# Revit family: 306_3370fe3ddf954dd49679af15ecbe6b
name_source: partatom
category: Pipe Accessories
units: mm (PartAtom-declared; Revit-internal decimal feet)

## family parameters
Always vertical = Yes
Cut with Voids When Loaded = No
Part Type = Valve - Breaks Into
Round Connector Dimension = Use Diameter
Shared = No
Work Plane-Based = No

## types (4) — shared parameters
CAT0 = Yes
Description = 2-way Control valve with pressure balanced plug VLE222, PN16 external thread
L2D_Min = 3048 mm
Manufacturer = ESBE
QmdConnectorList = 301;D;302;D
URL = http://www.esbe.eu
Z4 = 13 mm  [stored 0.0426509 ft]
Z5 = 4 mm  [stored 0.0131234 ft]
Z6 = 2 mm  [stored 0.00656168 ft]
Z7 = 15 mm  [stored 0.0492126 ft]
magiPartTypeId = 306
magiProductFamilyId = 3370fe3ddf954dd49679af15ecbe6b

## per-type parameters (varying)
- VLE222 PN16 G1 1/2 DN25-10: CenSd_D6_6=13 mm  [stored 0.0426509 ft]; D=25 mm; D1=29 mm; D13=13 mm  [stored 0.0426509 ft]; D2=24 mm; D3=21 mm; D4=19 mm; D5=20 mm  [stored 0.0656168 ft]; D6=15 mm  [stored 0.0492126 ft]; D7=11 mm; D8=5 mm  [stored 0.0164042 ft]; D9=5 mm  [stored 0.0164042 ft]; DN=20 mm  [stored 0.0656168 ft]; DN1=17 mm  [stored 0.0557743 ft]; DN2=15 mm  [stored 0.0492126 ft]; H3=78 mm; H4=34 mm  [stored 0.111549 ft]; L2=78 mm; L2D=105 mm; LT2=53 mm  [stored 0.173885 ft]; W2D=25 mm  [stored 0.082021 ft]; X1=3 mm  [stored 0.00984252 ft]; XN=11 mm; XN__ve=-11 mm; Z11=9 mm  [stored 0.0295276 ft]; Z14=39 mm; Z2=51 mm  [stored 0.167323 ft]; magiProductId=2265d16c8a8e4a0798807a2ac3ad55
- VLE222 PN16 G2 DN32-16: CenSd_D6_6=13 mm  [stored 0.0426509 ft]; D=32 mm; D1=29 mm; D13=13 mm  [stored 0.0426509 ft]; D2=24 mm; D3=21 mm; D4=19 mm; D5=20 mm  [stored 0.0656168 ft]; D6=15 mm  [stored 0.0492126 ft]; D7=11 mm; D8=5 mm  [stored 0.0164042 ft]; D9=5 mm  [stored 0.0164042 ft]; DN=25 mm  [stored 0.082021 ft]; DN1=21 mm; DN2=19 mm; H3=81 mm; H4=35 mm  [stored 0.114829 ft]; L2=78 mm; L2D=105 mm; LT2=53 mm  [stored 0.173885 ft]; W2D=32 mm  [stored 0.104987 ft]; X1=3 mm  [stored 0.00984252 ft]; XN=11 mm; XN__ve=-11 mm; Z11=9 mm  [stored 0.0295276 ft]; Z14=41 mm; Z2=53 mm  [stored 0.173885 ft]; magiProductId=eaebc783e35940a1959392541471b1
- VLE222 PN16 G2 3/4 DN50-38: CenSd_D6_6=19 mm; D=50 mm; D1=42 mm  [stored 0.137795 ft]; D13=18 mm; D2=34 mm  [stored 0.111549 ft]; D3=30 mm  [stored 0.0984252 ft]; D4=27 mm; D5=29 mm; D6=22 mm; D7=15 mm  [stored 0.0492126 ft]; D8=8 mm  [stored 0.0262467 ft]; D9=7 mm  [stored 0.0229659 ft]; DN=40 mm  [stored 0.131234 ft]; DN1=34 mm  [stored 0.111549 ft]; DN2=30 mm  [stored 0.0984252 ft]; H3=80 mm; H4=53 mm  [stored 0.173885 ft]; L2=111 mm; L2D=150 mm; LT2=75 mm; W2D=50 mm  [stored 0.164042 ft]; X1=5 mm  [stored 0.0164042 ft]; XN=15 mm  [stored 0.0492126 ft]; XN__ve=-15 mm  [stored -0.0492126 ft]; Z11=13 mm  [stored 0.0426509 ft]; Z14=30 mm  [stored 0.0984252 ft]; Z2=80 mm; magiProductId=a5fd4d7e4d3149f6a6e4df05a8dac0
- VLE222 PN16 G2 1/4 DN40-25: CenSd_D6_6=16 mm; D=40 mm; D1=36 mm; D13=16 mm; D2=29 mm; D3=26 mm; D4=24 mm; D5=25 mm  [stored 0.082021 ft]; D6=19 mm; D7=13 mm  [stored 0.0426509 ft]; D8=7 mm  [stored 0.0229659 ft]; D9=6 mm  [stored 0.019685 ft]; DN=30 mm  [stored 0.0984252 ft]; DN1=26 mm; DN2=23 mm; H3=78 mm; H4=42 mm  [stored 0.137795 ft]; L2=96 mm; L2D=130 mm; LT2=65 mm; W2D=40 mm  [stored 0.131234 ft]; X1=4 mm  [stored 0.0131234 ft]; XN=13 mm  [stored 0.0426509 ft]; XN__ve=-13 mm  [stored -0.0426509 ft]; Z11=11 mm; Z14=35 mm  [stored 0.114829 ft]; Z2=63 mm  [stored 0.206693 ft]; magiProductId=a6254704e78141fcb74e68cc524de8

note: column(s) folded — value = type name in every type: magiProductCode

note: [stored X ft] marks values corroborated as IEEE doubles in the binary element streams (Revit-internal decimal feet)

## geometry (parser evidence)
native form markers: Sweep x1
no freeform markers — native parametric forms only
